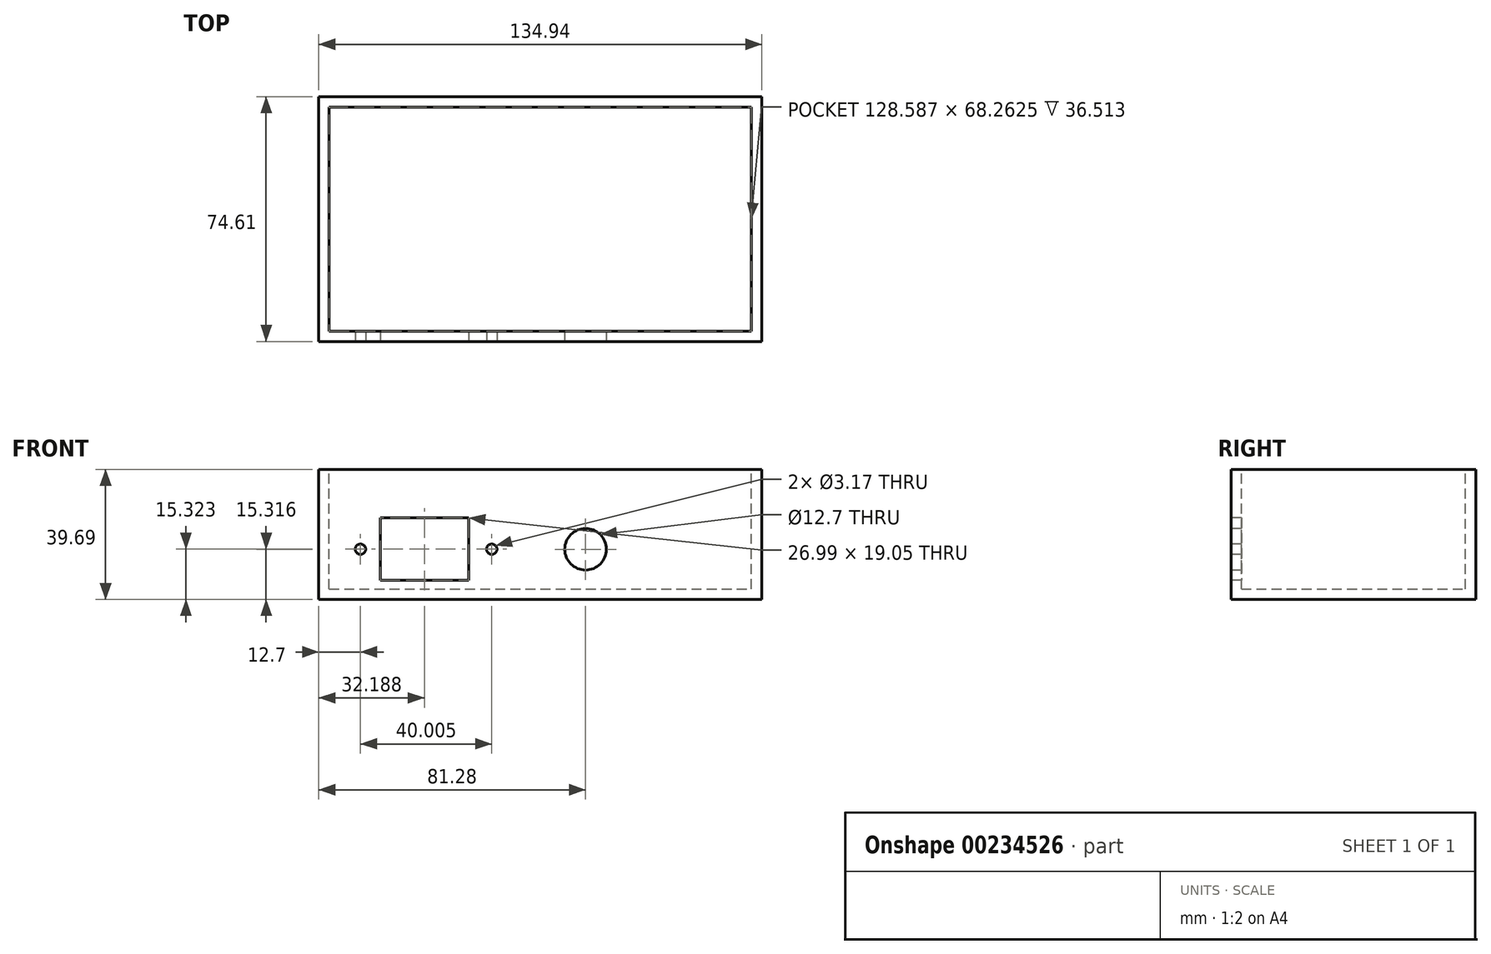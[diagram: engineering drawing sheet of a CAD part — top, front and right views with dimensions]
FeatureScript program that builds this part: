
annotation { "Feature Type Name" : "Feature", "Feature Type Description" : "" }
export const myFeature = defineFeature(function(context is Context, id is Id, definition is map)
    precondition{}
    {
        {
            var Q0;
            Q0=qCreatedBy(makeId("Front.planeOp"),FACE);
            var sketch = newSketch(context, id + "F0", { "sketchPlane" : qUnion([Q0])});
            skLineSegment(sketch, "E0.bottom", {"start": v(0, 0) * mm, "end": v(134.94, 0) * mm});
            skLineSegment(sketch, "E0.top", {"start": v(0, 39.69) * mm, "end": v(134.94, 39.69) * mm});
            skLineSegment(sketch, "E0.left", {"start": v(0, 0) * mm, "end": v(0, 39.69) * mm});
            skLineSegment(sketch, "E0.right", {"start": v(134.94, 0) * mm, "end": v(134.94, 39.69) * mm});
            skSolve(sketch);
        }
        {
            var Q0;
            Q0=makeQuery(id+"F0.imprint","IMPRINT",FACE,{"disambiguationData":[TD([[makeQuery(id+"F0.imprint","IMPRINT",EDGE,{"derivedFrom":sQuery(id+"F0.wireOp",EDGE,"E0.bottom")}),1.0]])]});
            extrude(context, id + "F1", {"entities" : qUnion([Q0]), "oppositeDirection" : true, "depth" : 74.61 * mm});
        }
        {
            var Q0;
            Q0=makeQuery(id+"F1.opExtrude","SWEPT_FACE",FACE,{"disambiguationData":[OSD([sQuery(id+"F0.wireOp",EDGE,"E0.top")])]});
            var sketch = newSketch(context, id + "F2", { "sketchPlane" : qUnion([Q0])});
            skLineSegment(sketch, "E1.bottom", {"start": v(3.18, 3.17) * mm, "end": v(131.76, 3.18) * mm});
            skLineSegment(sketch, "E1.top", {"start": v(3.17, 71.44) * mm, "end": v(131.76, 71.44) * mm});
            skLineSegment(sketch, "E1.left", {"start": v(3.18, 3.17) * mm, "end": v(3.17, 71.44) * mm});
            skLineSegment(sketch, "E1.right", {"start": v(131.76, 3.18) * mm, "end": v(131.76, 71.44) * mm});
            skSolve(sketch);
        }
        {
            var Q0;
            Q0=makeQuery(id+"F2.imprint","IMPRINT",FACE,{"disambiguationData":[TD([[makeQuery(id+"F2.imprint","IMPRINT",EDGE,{"derivedFrom":sQuery(id+"F2.wireOp",EDGE,"E1.bottom")}),1.0]])]});
            extrude(context, id + "F3", {"entities" : qUnion([Q0]), "operationType" : NewBodyOperationType.REMOVE, "oppositeDirection" : true, "depth" : 36.5 * mm});
        }
        {
            var Q0;
            Q0=makeQuery(id+"F1.opExtrude","CAP_FACE",FACE,{"disambiguationData":[OSD([sQuery(id+"F0.wireOp",EDGE,"E0.bottom"),sQuery(id+"F0.wireOp",EDGE,"E0.top"),sQuery(id+"F0.wireOp",EDGE,"E0.left"),sQuery(id+"F0.wireOp",EDGE,"E0.right")])],"isStart":true});
            var sketch = newSketch(context, id + "F4", { "sketchPlane" : qUnion([Q0])});
            skLineSegment(sketch, "E2.bottom", {"start": v(18.7, 24.85) * mm, "end": v(45.68, 24.85) * mm});
            skLineSegment(sketch, "E2.top", {"start": v(18.7, 5.8) * mm, "end": v(45.68, 5.8) * mm});
            skLineSegment(sketch, "E2.left", {"start": v(18.7, 24.85) * mm, "end": v(18.7, 5.8) * mm});
            skLineSegment(sketch, "E2.right", {"start": v(45.68, 24.85) * mm, "end": v(45.68, 5.8) * mm});
            skLineSegment(sketch, "E3", {"start": v(18.7, 15.32) * mm, "end": v(45.68, 15.32) * mm, "construction": true});
            skCircle(sketch, "E4", {"center": v(12.7, 15.32) * mm, "radius": 1.59 * mm});
            skCircle(sketch, "E5.1.0.0", {"center": v(52.7, 15.32) * mm, "radius": 1.59 * mm});
            skLineSegment(sketch, "E5.direction1", {"start": v(12.7, 15.32) * mm, "end": v(52.7, 15.32) * mm, "construction": true});
            skCircle(sketch, "E6", {"center": v(81.28, 15.32) * mm, "radius": 6.35 * mm});
            skSolve(sketch);
        }
        {
            var Q0;
            Q0=makeQuery(id+"F4.imprint","IMPRINT",FACE,{"disambiguationData":[TD([[makeQuery(id+"F4.imprint","IMPRINT",EDGE,{"derivedFrom":sQuery(id+"F4.wireOp",EDGE,"E4")}),1.0]])]});
            var Q1;
            Q1=makeQuery(id+"F4.imprint","IMPRINT",FACE,{"disambiguationData":[TD([[makeQuery(id+"F4.imprint","IMPRINT",EDGE,{"derivedFrom":sQuery(id+"F4.wireOp",EDGE,"E5.1.0.0")}),1.0]])]});
            var Q2;
            Q2=makeQuery(id+"F4.imprint","IMPRINT",FACE,{"disambiguationData":[TD([[makeQuery(id+"F4.imprint","IMPRINT",EDGE,{"derivedFrom":sQuery(id+"F4.wireOp",EDGE,"E2.bottom")}),-1.0]])]});
            extrude(context, id + "F5", {"entities" : qUnion([Q0, Q1, Q2]), "operationType" : NewBodyOperationType.REMOVE, "oppositeDirection" : true, "depth" : 6.35 * mm});
        }
        {
            var Q0;
            Q0=makeQuery(id+"F1.opExtrude","CAP_FACE",FACE,{"disambiguationData":[OSD([sQuery(id+"F0.wireOp",EDGE,"E0.bottom"),sQuery(id+"F0.wireOp",EDGE,"E0.top"),sQuery(id+"F0.wireOp",EDGE,"E0.left"),sQuery(id+"F0.wireOp",EDGE,"E0.right")])],"isStart":true});
            var sketch = newSketch(context, id + "F6", { "sketchPlane" : qUnion([Q0])});
            skCircle(sketch, "E7", {"center": v(81.28, 15.32) * mm, "radius": 6.35 * mm});
            skSolve(sketch);
        }
        {
            var Q0;
            Q0=makeQuery(id+"F6.imprint","IMPRINT",FACE,{"disambiguationData":[TD([[makeQuery(id+"F6.imprint","IMPRINT",EDGE,{"derivedFrom":sQuery(id+"F6.wireOp",EDGE,"E7")}),1.0]])]});
            extrude(context, id + "F7", {"entities" : qUnion([Q0]), "operationType" : NewBodyOperationType.REMOVE, "oppositeDirection" : true, "depth" : 6.35 * mm});
        }
    });
